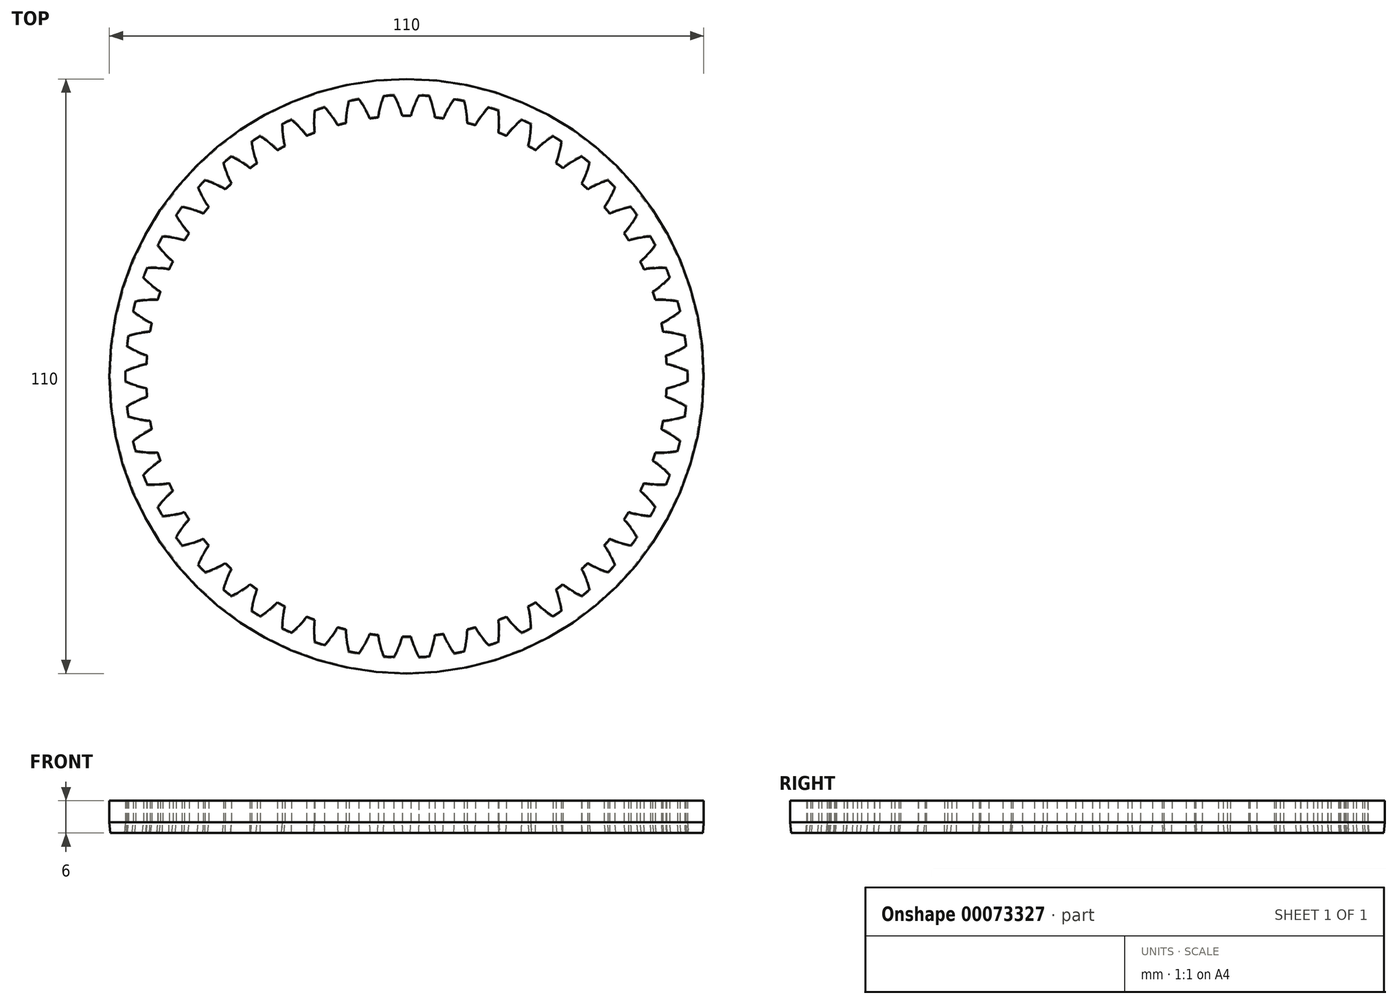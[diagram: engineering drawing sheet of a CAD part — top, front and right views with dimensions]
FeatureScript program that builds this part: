
annotation { "Feature Type Name" : "Feature", "Feature Type Description" : "" }
export const myFeature = defineFeature(function(context is Context, id is Id, definition is map)
    precondition{}
    {
        {
            assignVariable(context, id + "F0", {"name" : "z1", "anyValue" : 50});
        }
        {
            assignVariable(context, id + "F1", {"name" : "b1", "anyValue" : 4});
        }
        {
            assignVariable(context, id + "F2", {"name" : "b2", "anyValue" : 2});
        }
        {
            var Q0;
            Q0=qCreatedBy(makeId("Top.planeOp"),FACE);
            var sketch = newSketch(context, id + "F3", { "sketchPlane" : qUnion([Q0])});
            skCircle(sketch, "E0", {"center": v(0, 0) * mm, "radius": 50 * mm, "construction": true});
            skCircle(sketch, "E1", {"center": v(0, 0) * mm, "radius": 52 * mm, "construction": true});
            skCircle(sketch, "E2", {"center": v(0, 0) * mm, "radius": 48 * mm, "construction": true});
            skCircle(sketch, "E3", {"center": v(0, 0) * mm, "radius": 46.98 * mm, "construction": true});
            skLineSegment(sketch, "E4", {"start": v(-1.63, 51.97) * mm, "end": v(0, 0) * mm, "construction": true});
            skLineSegment(sketch, "E5", {"start": v(1.63, 51.97) * mm, "end": v(0, 0) * mm, "construction": true});
            skLineSegment(sketch, "E6", {"start": v(-17.45, 43.62) * mm, "end": v(0, 0) * mm, "construction": true});
            skLineSegment(sketch, "E7", {"start": v(0, 0) * mm, "end": v(17.45, 43.62) * mm, "construction": true});
            skPoint(sketch, "E8", {"position": v(-1.57, 49.98) * mm});
            skPoint(sketch, "E9", {"position": v(1.57, 49.98) * mm});
            skCircle(sketch, "E10", {"center": v(-17.45, 43.62) * mm, "radius": 17.1 * mm, "construction": true});
            skCircle(sketch, "E11", {"center": v(17.45, 43.62) * mm, "radius": 17.1 * mm, "construction": true});
            skCircle(sketch, "E12", {"center": v(-17.45, 43.62) * mm, "radius": 17.25 * mm, "construction": true});
            skCircle(sketch, "E13", {"center": v(17.45, 43.62) * mm, "radius": 17.25 * mm, "construction": true});
            skCircle(sketch, "E14", {"center": v(0, 0) * mm, "radius": 48.15 * mm, "construction": true});
            skPoint(sketch, "E15", {"position": v(-0.8, 48.14) * mm});
            skPoint(sketch, "E16", {"position": v(0.8, 48.14) * mm});
            skPoint(sketch, "E17", {"position": v(-2.34, 51.95) * mm});
            skPoint(sketch, "E18", {"position": v(2.34, 51.95) * mm});
            skArc(sketch, "E19", {"start": v(0.8, 48.14) * mm, "mid": v(0, 48.15) * mm, "end": v(-0.8, 48.14) * mm});
            skArc(sketch, "E20", {"start": v(-0.8, 48.14) * mm, "mid": v(-1.46, 50.1) * mm, "end": v(-2.34, 51.95) * mm});
            skArc(sketch, "E21", {"start": v(2.34, 51.95) * mm, "mid": v(1.46, 50.1) * mm, "end": v(0.8, 48.14) * mm});
            skArc(sketch, "E22", {"start": v(2.34, 51.95) * mm, "mid": v(0, 52) * mm, "end": v(-2.34, 51.95) * mm});
            skSolve(sketch);
        }
        {
            var Q0;
            Q0=makeQuery(id+"F3.imprint","IMPRINT",FACE,{"disambiguationData":[TD([[makeQuery(id+"F3.imprint","IMPRINT",EDGE,{"derivedFrom":sQuery(id+"F3.wireOp",EDGE,"E19")}),-1.0]])]});
            extrude(context, id + "F4", {"entities" : qUnion([Q0]), "depth" : (getVariable(context, 'b1')) * mm});
        }
        {
            var Q0;
            Q0=qCreatedBy(makeId("Front.planeOp"),FACE);
            var sketch = newSketch(context, id + "F5", { "sketchPlane" : qUnion([Q0])});
            skLineSegment(sketch, "E23", {"start": v(0, 0) * mm, "end": v(0, 6) * mm, "construction": true});
            skSolve(sketch);
        }
        {
            var Q0;
            Q0=makeQuery(id+"F4.opExtrude","SWEPT_BODY",BODY,{"disambiguationData":[OSD([sQuery(id+"F3.wireOp",EDGE,"E19"),sQuery(id+"F3.wireOp",EDGE,"E20"),sQuery(id+"F3.wireOp",EDGE,"E21"),sQuery(id+"F3.wireOp",EDGE,"E22")])]});
            var Q1;
            Q1=sQuery(id+"F5.wireOp",EDGE,"E23");
            circularPattern(context, id + "F6", {"entities" : qUnion([Q0]), "axis" : qUnion([Q1]), "angle" : (360 / getVariable(context, 'z1')) * degree, "instanceCount" : getVariable(context, 'z1')});
        }
        {
            var Q0;
            Q0=qCreatedBy(makeId("Top.planeOp"),FACE);
            var sketch = newSketch(context, id + "F7", { "sketchPlane" : qUnion([Q0])});
            skCircle(sketch, "E24", {"center": v(0, 0) * mm, "radius": 55 * mm});
            skCircle(sketch, "E25", {"center": v(0, 0) * mm, "radius": 52 * mm});
            skSolve(sketch);
        }
        {
            var Q0;
            Q0=makeQuery(id+"F7.imprint","IMPRINT",FACE,{"disambiguationData":[TD([[makeQuery(id+"F7.imprint","IMPRINT",EDGE,{"derivedFrom":sQuery(id+"F7.wireOp",EDGE,"E24")}),1.0]])]});
            extrude(context, id + "F8", {"entities" : qUnion([Q0]), "operationType" : NewBodyOperationType.ADD, "depth" : (getVariable(context, 'b1')) * mm});
        }
        {
            var Q0;
            {var subQ0=makeQuery(id+"F4.opExtrude","CAP_FACE",FACE,{"disambiguationData":[OSD([sQuery(id+"F3.wireOp",EDGE,"E19"),sQuery(id+"F3.wireOp",EDGE,"E20"),sQuery(id+"F3.wireOp",EDGE,"E21"),sQuery(id+"F3.wireOp",EDGE,"E22")])],"isStart":true});Q0=makeQuery(id+"F8.boolean.opBoolean","MERGE",FACE,{"derivedFrom":[subQ0,makeQuery(id+"F6.opPattern","COPY",FACE,{"derivedFrom":subQ0,"instanceName":"1"}),makeQuery(id+"F6.opPattern","COPY",FACE,{"derivedFrom":subQ0,"instanceName":"2"}),makeQuery(id+"F6.opPattern","COPY",FACE,{"derivedFrom":subQ0,"instanceName":"3"}),makeQuery(id+"F6.opPattern","COPY",FACE,{"derivedFrom":subQ0,"instanceName":"4"}),makeQuery(id+"F6.opPattern","COPY",FACE,{"derivedFrom":subQ0,"instanceName":"5"}),makeQuery(id+"F6.opPattern","COPY",FACE,{"derivedFrom":subQ0,"instanceName":"6"}),makeQuery(id+"F6.opPattern","COPY",FACE,{"derivedFrom":subQ0,"instanceName":"7"}),makeQuery(id+"F6.opPattern","COPY",FACE,{"derivedFrom":subQ0,"instanceName":"8"}),makeQuery(id+"F6.opPattern","COPY",FACE,{"derivedFrom":subQ0,"instanceName":"9"}),makeQuery(id+"F6.opPattern","COPY",FACE,{"derivedFrom":subQ0,"instanceName":"10"}),makeQuery(id+"F6.opPattern","COPY",FACE,{"derivedFrom":subQ0,"instanceName":"11"}),makeQuery(id+"F6.opPattern","COPY",FACE,{"derivedFrom":subQ0,"instanceName":"12"}),makeQuery(id+"F6.opPattern","COPY",FACE,{"derivedFrom":subQ0,"instanceName":"13"}),makeQuery(id+"F6.opPattern","COPY",FACE,{"derivedFrom":subQ0,"instanceName":"14"}),makeQuery(id+"F6.opPattern","COPY",FACE,{"derivedFrom":subQ0,"instanceName":"15"}),makeQuery(id+"F6.opPattern","COPY",FACE,{"derivedFrom":subQ0,"instanceName":"16"}),makeQuery(id+"F6.opPattern","COPY",FACE,{"derivedFrom":subQ0,"instanceName":"17"}),makeQuery(id+"F6.opPattern","COPY",FACE,{"derivedFrom":subQ0,"instanceName":"18"}),makeQuery(id+"F6.opPattern","COPY",FACE,{"derivedFrom":subQ0,"instanceName":"19"}),makeQuery(id+"F6.opPattern","COPY",FACE,{"derivedFrom":subQ0,"instanceName":"20"}),makeQuery(id+"F6.opPattern","COPY",FACE,{"derivedFrom":subQ0,"instanceName":"21"}),makeQuery(id+"F6.opPattern","COPY",FACE,{"derivedFrom":subQ0,"instanceName":"22"}),makeQuery(id+"F6.opPattern","COPY",FACE,{"derivedFrom":subQ0,"instanceName":"23"}),makeQuery(id+"F6.opPattern","COPY",FACE,{"derivedFrom":subQ0,"instanceName":"24"}),makeQuery(id+"F6.opPattern","COPY",FACE,{"derivedFrom":subQ0,"instanceName":"25"}),makeQuery(id+"F6.opPattern","COPY",FACE,{"derivedFrom":subQ0,"instanceName":"26"}),makeQuery(id+"F6.opPattern","COPY",FACE,{"derivedFrom":subQ0,"instanceName":"27"}),makeQuery(id+"F6.opPattern","COPY",FACE,{"derivedFrom":subQ0,"instanceName":"28"}),makeQuery(id+"F6.opPattern","COPY",FACE,{"derivedFrom":subQ0,"instanceName":"29"}),makeQuery(id+"F6.opPattern","COPY",FACE,{"derivedFrom":subQ0,"instanceName":"30"}),makeQuery(id+"F6.opPattern","COPY",FACE,{"derivedFrom":subQ0,"instanceName":"31"}),makeQuery(id+"F6.opPattern","COPY",FACE,{"derivedFrom":subQ0,"instanceName":"32"}),makeQuery(id+"F6.opPattern","COPY",FACE,{"derivedFrom":subQ0,"instanceName":"33"}),makeQuery(id+"F6.opPattern","COPY",FACE,{"derivedFrom":subQ0,"instanceName":"34"}),makeQuery(id+"F6.opPattern","COPY",FACE,{"derivedFrom":subQ0,"instanceName":"35"}),makeQuery(id+"F6.opPattern","COPY",FACE,{"derivedFrom":subQ0,"instanceName":"36"}),makeQuery(id+"F6.opPattern","COPY",FACE,{"derivedFrom":subQ0,"instanceName":"37"}),makeQuery(id+"F6.opPattern","COPY",FACE,{"derivedFrom":subQ0,"instanceName":"38"}),makeQuery(id+"F6.opPattern","COPY",FACE,{"derivedFrom":subQ0,"instanceName":"39"}),makeQuery(id+"F6.opPattern","COPY",FACE,{"derivedFrom":subQ0,"instanceName":"40"}),makeQuery(id+"F6.opPattern","COPY",FACE,{"derivedFrom":subQ0,"instanceName":"41"}),makeQuery(id+"F6.opPattern","COPY",FACE,{"derivedFrom":subQ0,"instanceName":"42"}),makeQuery(id+"F6.opPattern","COPY",FACE,{"derivedFrom":subQ0,"instanceName":"43"}),makeQuery(id+"F6.opPattern","COPY",FACE,{"derivedFrom":subQ0,"instanceName":"44"}),makeQuery(id+"F6.opPattern","COPY",FACE,{"derivedFrom":subQ0,"instanceName":"45"}),makeQuery(id+"F6.opPattern","COPY",FACE,{"derivedFrom":subQ0,"instanceName":"46"}),makeQuery(id+"F6.opPattern","COPY",FACE,{"derivedFrom":subQ0,"instanceName":"47"}),makeQuery(id+"F6.opPattern","COPY",FACE,{"derivedFrom":subQ0,"instanceName":"48"}),makeQuery(id+"F6.opPattern","COPY",FACE,{"derivedFrom":subQ0,"instanceName":"49"}),makeQuery(id+"F8.opExtrude","CAP_FACE",FACE,{"disambiguationData":[OSD([sQuery(id+"F7.wireOp",EDGE,"E24"),sQuery(id+"F7.wireOp",EDGE,"cae7718c-7b55-44ed-a312-4b7a1dedc630")])],"isStart":true})]});}
            extrude(context, id + "F9", {"entities" : qUnion([Q0]), "operationType" : NewBodyOperationType.ADD, "depth" : (getVariable(context, 'b2')) * mm, "hasDraft" : true, "draftAngle" : 5 * degree, "draftPullDirection" : true});
        }
    });
